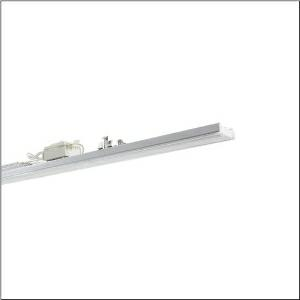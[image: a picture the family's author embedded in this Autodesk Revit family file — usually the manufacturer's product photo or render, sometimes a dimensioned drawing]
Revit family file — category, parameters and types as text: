
# Revit family: licross_11_recessed_mo_51tl12dn455gd
name_source: partatom
category: Lighting Fixtures
units: mm (PartAtom-declared; Revit-internal decimal feet)

## family parameters
Cut with Voids When Loaded = No
Host = Face
Light Source = No
Part Type = Normal
Room Calculation Point = No
Round Connector Dimension = Use Diameter
Shared = No

## types (1)
- --- (1 x LED, 860 lm, 5.3 W, 4000K)
    Apparent Load = 5 VA
    CIE Flux Codes = 67 92 99 100 100
    Color Rendering = 80
    Color Temperature = 4000K
    Default Elevation = 1800 mm
    Description = Licross 11 Recessed MO, luminaire insert, of sheet steel, coil coated, white, length: 1.500mm, width: 66mm, height: 67mm, LED rated luminous flux: 5.700lm, light colour: 840, SDCM (Standard Deviation of Colour Matching)MacAdam ≤ 2 SDCM (initial), control gear: DALI 2 (for two DALI lines), with plug, 6-pole, with phase selection, mains connection: 220..240V, AC/DC, 0/50..60Hz, rated input power: 30W, without changeover relay, for emergency light function, for central battery installations according to EN 60598-2-22, internal wiring halogen-free, primary optical cover: cover, of PMMA, light emission: direct distribution, primary light characteristic: symmetric, protection rating (complete): IP40, insulation class (complete): insulation class I (protective earthing), certification: CE, ENEC, VDE, UKCA, protection symbol: D if used in an environment without relevant dust loads with corresponding accessories, impact resistance: IK06, permissible ambient temperature for indoor applications: -25..+45°C, standard: EN 60598-2-22, corresponds to IFS (International Featured Standards) requirements for safety and quality in the food industry, reducing of maximum allowable ambient temperature of 5°C with ceiling mounting, LABS conformity tested according to VDMA 24364:2018-05, The light source and the operating device comply with the requirements of the Ecodesign Regulation (EU) 2019/2020 and are replaceable in accordance with this regulation, packaging unit: 1 piece
    Height = 58 mm
    Lamp = 1 x LED
    Lamp Light Flux = 860 lm
    Lamp Power = 5.3 W
    Lamp count = 1
    Length = 1500 mm
    Luminous efficacy = 162 lm/W
    Manufacturer = Siteco
    ModVariant = No
    Model = 51TL12DN455GD
    Mounting Place = Ceiling
    Mounting Type = Pendant
    Number of Poles = 1
    OnlyDefault = Yes
    Power Factor = 1
    Product Name = Licross 11 Recessed MO
    Product group = luminaire insert | ceiling pendant
    ProductGroupID = 901
    Protection Class = Protection class I
    Protection Degree = IP 40
    RLX_Detail_Level = 1
    RLX_Emergency_Light_Flux = 0 lm
    RLX_Emergency_Type = 0
    RLX_Emergency_Type_DB = No
    RlxData = <blob elided: 24733 chars, md5=e49debda>
    Socket = socket
    Standby Power = 0 W
    System Light Flux = 860 lm
    System Power = 5 W
    Type Comments = : DC mode (central or group accumulator) initial emergency light level
    Type Image = l_1296930.jpg
    URL = http://relux.com
    VarID = @adj_091445
    Voltage = 0 V
    Weight = 0.00 kg
    Width = 66 mm

## geometry (parser evidence)
native form markers: Blend x4, Sweep x10
no freeform markers — native parametric forms only
